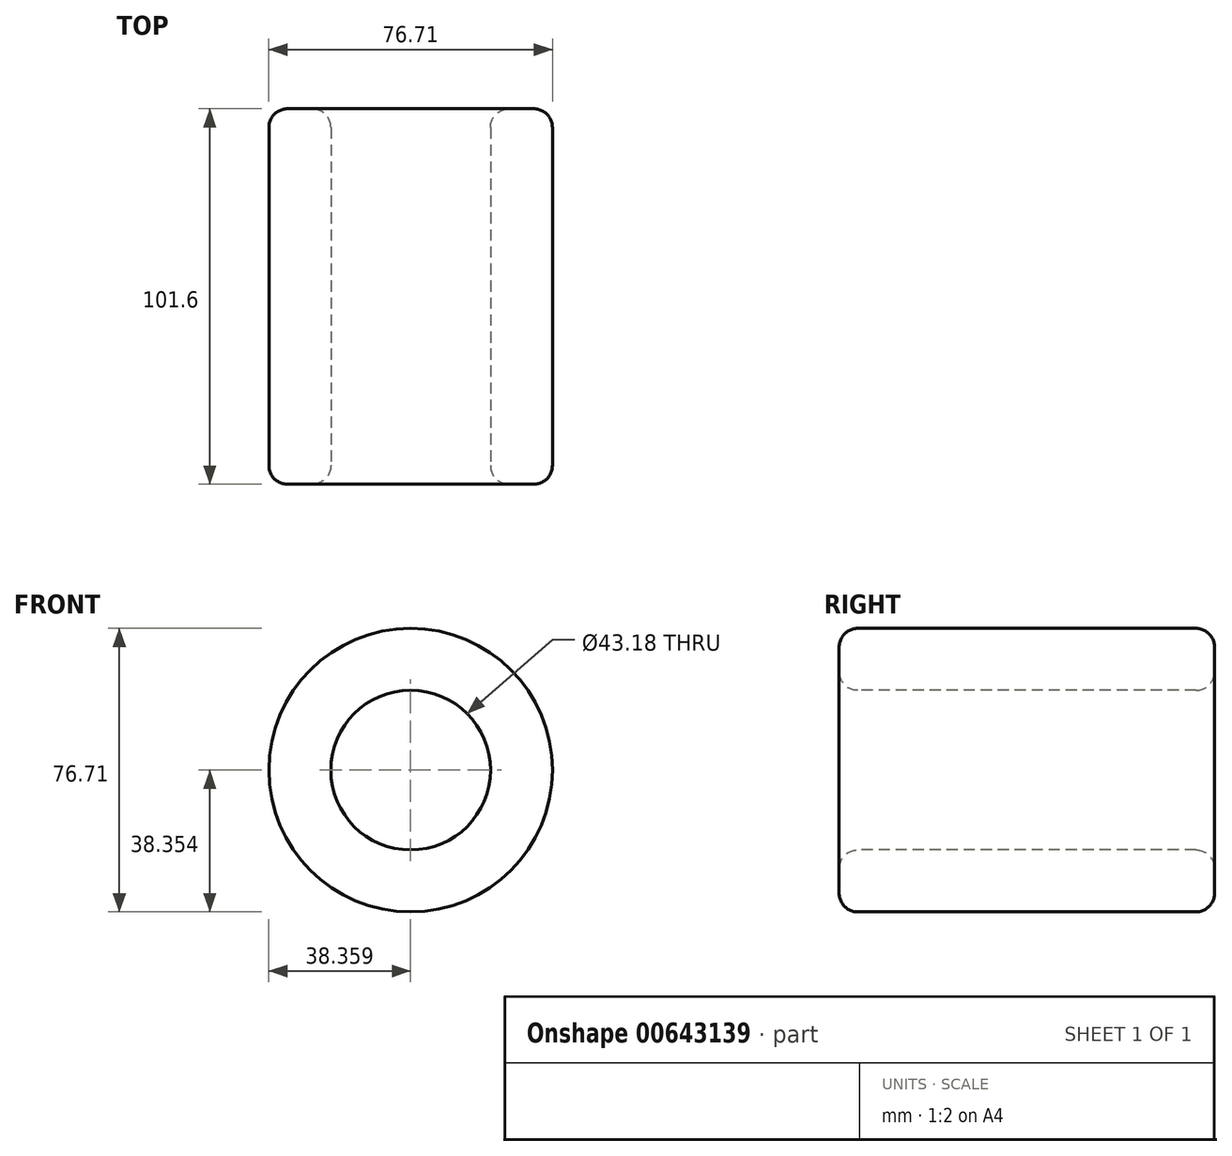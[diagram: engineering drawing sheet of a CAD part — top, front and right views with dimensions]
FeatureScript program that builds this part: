
annotation { "Feature Type Name" : "Feature", "Feature Type Description" : "" }
export const myFeature = defineFeature(function(context is Context, id is Id, definition is map)
    precondition{}
    {
        {
            var Q0;
            Q0=qCreatedBy(makeId("Front.planeOp"),FACE);
            var sketch = newSketch(context, id + "F0", { "sketchPlane" : qUnion([Q0])});
            skCircle(sketch, "E0", {"center": v(-10.85, 16.5) * mm, "radius": 38.36 * mm});
            skSolve(sketch);
        }
        {
            var Q0;
            Q0=makeQuery(id+"F0.imprint","IMPRINT",FACE,{"disambiguationData":[TD([[makeQuery(id+"F0.imprint","IMPRINT",EDGE,{"derivedFrom":sQuery(id+"F0.wireOp",EDGE,"E0")}),1.0]])]});
            extrude(context, id + "F1", {"entities" : qUnion([Q0]), "depth" : 101.6 * mm, "offsetDistance" : 25.4 * mm});
        }
        {
            var Q0;
            Q0=makeQuery(id+"F1.opExtrude","CAP_FACE",FACE,{"disambiguationData":[OSD([sQuery(id+"F0.wireOp",EDGE,"E0")])],"isStart":false});
            var sketch = newSketch(context, id + "F2", { "sketchPlane" : qUnion([Q0])});
            skCircle(sketch, "E1", {"center": v(-10.85, 16.5) * mm, "radius": 23.08 * mm});
            skSolve(sketch);
        }
        {
            var Q0;
            Q0=sQuery(id+"F2.wireOp",VERTEX,"E1.center");
            var Q1;
            Q1=makeQuery(id+"F1.opExtrude","SWEPT_BODY",BODY,{"disambiguationData":[OSD([sQuery(id+"F0.wireOp",EDGE,"E0")])]});
            hole(context, id + "F3", {"style" : HoleStyle.SIMPLE, "endStyle" : HoleEndStyle.THROUGH, "holeDiameter" : 43.18 * mm, "majorDiameter" : 6.35 * mm, "isTappedThrough" : true, "tappedDepth" : 12.7 * mm, "tapClearance" : 3, "locations" : qUnion([Q0]), "scope" : qUnion([Q1])});
        }
        {
            var Q0;
            Q0=makeQuery(id+"F1.opExtrude","CAP_FACE",FACE,{"disambiguationData":[OSD([sQuery(id+"F0.wireOp",EDGE,"E0")])],"isStart":true});
            fillet(context, id + "F4", {"entities" : qUnion([Q0]), "radius" : 5.08 * mm, "tangentPropagation" : true, "allowEdgeOverflow" : false});
        }
        {
            var Q0;
            Q0=makeQuery(id+"F1.opExtrude","CAP_FACE",FACE,{"disambiguationData":[OSD([sQuery(id+"F0.wireOp",EDGE,"E0")])],"isStart":false});
            fillet(context, id + "F5", {"entities" : qUnion([Q0]), "radius" : 5.08 * mm, "tangentPropagation" : true, "allowEdgeOverflow" : false});
        }
    });
